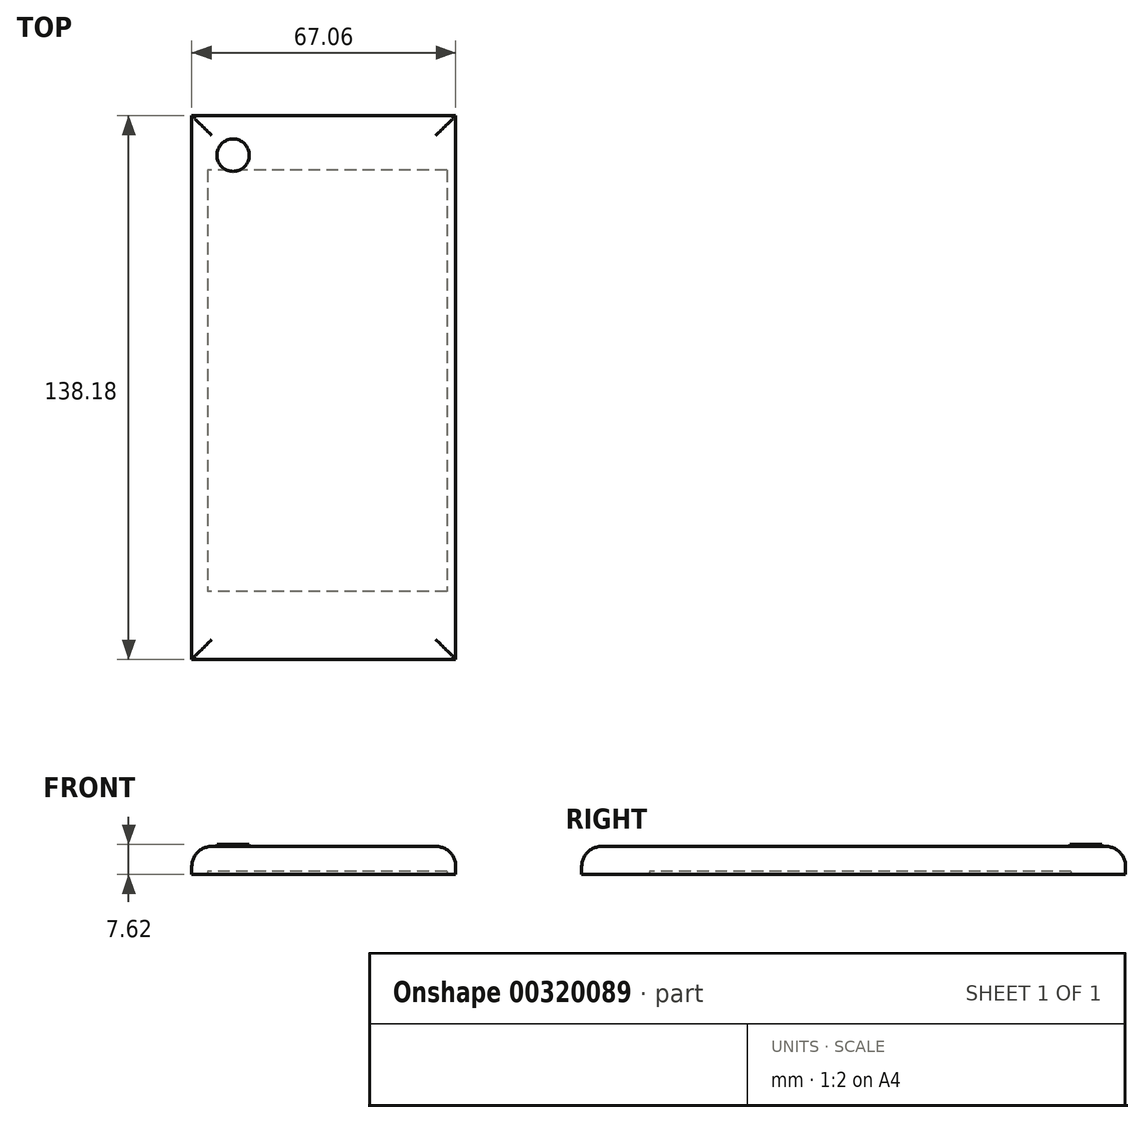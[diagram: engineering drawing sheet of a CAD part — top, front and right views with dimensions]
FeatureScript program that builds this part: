
annotation { "Feature Type Name" : "Feature", "Feature Type Description" : "" }
export const myFeature = defineFeature(function(context is Context, id is Id, definition is map)
    precondition{}
    {
        {
            var Q0;
            Q0=qCreatedBy(makeId("Top.planeOp"),FACE);
            var sketch = newSketch(context, id + "F0", { "sketchPlane" : qUnion([Q0])});
            skLineSegment(sketch, "E0.bottom", {"start": v(-28.3, -44.44) * mm, "end": v(38.75, -44.44) * mm});
            skLineSegment(sketch, "E0.top", {"start": v(-28.3, 93.74) * mm, "end": v(38.75, 93.74) * mm});
            skLineSegment(sketch, "E0.left", {"start": v(-28.3, -44.44) * mm, "end": v(-28.3, 93.74) * mm});
            skLineSegment(sketch, "E0.right", {"start": v(38.75, -44.44) * mm, "end": v(38.75, 93.74) * mm});
            skSolve(sketch);
        }
        {
            var Q0;
            Q0=makeQuery(id+"F0.imprint","IMPRINT",FACE,{"disambiguationData":[TD([[makeQuery(id+"F0.imprint","IMPRINT",EDGE,{"derivedFrom":sQuery(id+"F0.wireOp",EDGE,"E0.bottom")}),1.0]])]});
            extrude(context, id + "F1", {"entities" : qUnion([Q0]), "depth" : 7.11 * mm});
        }
        {
            var Q0;
            Q0=makeQuery(id+"F1.opExtrude","CAP_EDGE",EDGE,{"disambiguationData":[OSD([sQuery(id+"F0.wireOp",EDGE,"E0.right")])],"isStart":false});
            var Q1;
            Q1=makeQuery(id+"F1.opExtrude","CAP_EDGE",EDGE,{"disambiguationData":[OSD([sQuery(id+"F0.wireOp",EDGE,"E0.bottom")])],"isStart":false});
            var Q2;
            Q2=makeQuery(id+"F1.opExtrude","CAP_EDGE",EDGE,{"disambiguationData":[OSD([sQuery(id+"F0.wireOp",EDGE,"E0.left")])],"isStart":false});
            var Q3;
            Q3=makeQuery(id+"F1.opExtrude","CAP_EDGE",EDGE,{"disambiguationData":[OSD([sQuery(id+"F0.wireOp",EDGE,"E0.top")])],"isStart":false});
            fillet(context, id + "F2", {"entities" : qUnion([Q0, Q1, Q2, Q3]), "radius" : 5.08 * mm, "tangentPropagation" : true, "allowEdgeOverflow" : false});
        }
        {
            var Q0;
            Q0=makeQuery(id+"F1.opExtrude","CAP_FACE",FACE,{"disambiguationData":[OSD([sQuery(id+"F0.wireOp",EDGE,"E0.bottom"),sQuery(id+"F0.wireOp",EDGE,"E0.top"),sQuery(id+"F0.wireOp",EDGE,"E0.left"),sQuery(id+"F0.wireOp",EDGE,"E0.right")])],"isStart":false});
            var sketch = newSketch(context, id + "F3", { "sketchPlane" : qUnion([Q0])});
            skCircle(sketch, "E1", {"center": v(-17.82, 83.66) * mm, "radius": 4.11 * mm});
            skSolve(sketch);
        }
        {
            var Q0;
            Q0 = qSketchRegion(id + "F3", true);
            extrude(context, id + "F4", {"entities" : qUnion([Q0]), "operationType" : NewBodyOperationType.ADD, "depth" : 0.5 * mm});
        }
        {
            var Q0;
            Q0=makeQuery(id+"F1.opExtrude","CAP_FACE",FACE,{"disambiguationData":[OSD([sQuery(id+"F0.wireOp",EDGE,"E0.bottom"),sQuery(id+"F0.wireOp",EDGE,"E0.top"),sQuery(id+"F0.wireOp",EDGE,"E0.left"),sQuery(id+"F0.wireOp",EDGE,"E0.right")])],"isStart":true});
            var sketch = newSketch(context, id + "F5", { "sketchPlane" : qUnion([Q0])});
            skLineSegment(sketch, "E2.bottom", {"start": v(36.5, -79.88) * mm, "end": v(-24.35, -79.88) * mm});
            skLineSegment(sketch, "E2.top", {"start": v(36.5, 27.19) * mm, "end": v(-24.35, 27.19) * mm});
            skLineSegment(sketch, "E2.left", {"start": v(36.5, -79.88) * mm, "end": v(36.5, 27.19) * mm});
            skLineSegment(sketch, "E2.right", {"start": v(-24.35, -79.88) * mm, "end": v(-24.35, 27.19) * mm});
            skSolve(sketch);
        }
        {
            var Q0;
            Q0 = qSketchRegion(id + "F5", true);
            extrude(context, id + "F6", {"entities" : qUnion([Q0]), "operationType" : NewBodyOperationType.REMOVE, "oppositeDirection" : true, "depth" : 0.76 * mm});
        }
    });
